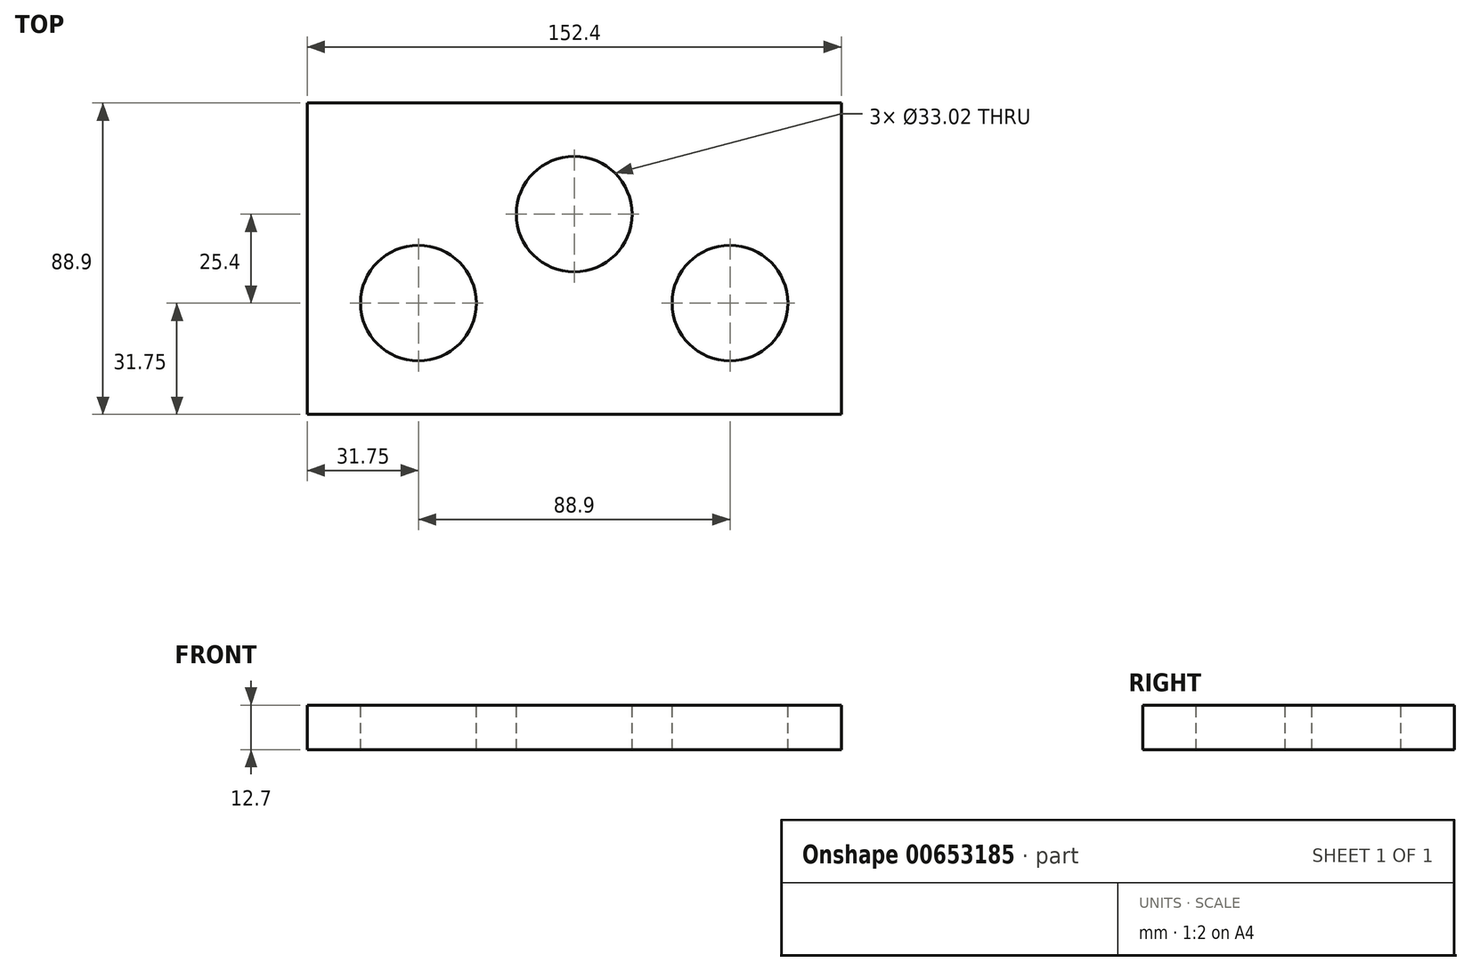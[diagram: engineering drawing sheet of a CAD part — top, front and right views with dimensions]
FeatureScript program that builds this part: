
annotation { "Feature Type Name" : "Feature", "Feature Type Description" : "" }
export const myFeature = defineFeature(function(context is Context, id is Id, definition is map)
    precondition{}
    {
        {
            var Q0;
            Q0=qCreatedBy(makeId("Top.planeOp"),FACE);
            var sketch = newSketch(context, id + "F0", { "sketchPlane" : qUnion([Q0])});
            skLineSegment(sketch, "E0.bottom", {"start": v(-76.2, -44.45) * mm, "end": v(76.2, -44.45) * mm});
            skLineSegment(sketch, "E0.top", {"start": v(-76.2, 44.45) * mm, "end": v(76.2, 44.45) * mm});
            skLineSegment(sketch, "E0.left", {"start": v(-76.2, -44.45) * mm, "end": v(-76.2, 44.45) * mm});
            skLineSegment(sketch, "E0.right", {"start": v(76.2, -44.45) * mm, "end": v(76.2, 44.45) * mm});
            skPoint(sketch, "E0.middle", {"position": v(0, 12.7) * mm});
            skCircle(sketch, "E1", {"center": v(-44.45, -12.7) * mm, "radius": 16.51 * mm});
            skCircle(sketch, "E2", {"center": v(0, 12.7) * mm, "radius": 16.51 * mm});
            skCircle(sketch, "E3", {"center": v(44.45, -12.7) * mm, "radius": 16.51 * mm});
            skSolve(sketch);
        }
        {
            var Q0;
            Q0=makeQuery(id+"F0.imprint","IMPRINT",FACE,{"disambiguationData":[TD([[makeQuery(id+"F0.imprint","IMPRINT",EDGE,{"derivedFrom":sQuery(id+"F0.wireOp",EDGE,"E0.bottom")}),1.0]])]});
            extrude(context, id + "F1", {"entities" : qUnion([Q0]), "oppositeDirection" : true, "depth" : 12.7 * mm, "offsetDistance" : 25.4 * mm});
        }
    });
